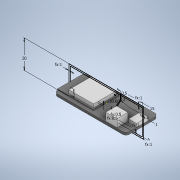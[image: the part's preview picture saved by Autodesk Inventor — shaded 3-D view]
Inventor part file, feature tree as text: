
AUTODESK INVENTOR PART (.ipt)
format: ipt  version: 2020 (Build 240168000, 168)  size: 187,904 bytes
history: native  units: in
note: dims shown in document units (in); Inventor stores cm internally (conversion verified against a paired STEP export)
features: extrude x6, sketch x2, fillet x1
ambient origin geometry x8: Origin, YZ Plane, XZ Plane, XY Plane, X Axis, Y Axis, Z Axis, Center Point
bodies: Solid1 (feature_tree)
feature tree (9):
  sketch  "Sketch1"  dims[d0=2.0079in d1=0.0689in d2=0.0315in]
  extrude  "PCB"  Depth=0.0689in
  fillet  "Fillet1"  Radius=0.0315in
  extrude  "ESP32PCB"  Depth=0.6949in
  extrude  "ESP32Shied"  Depth=0.0925in
  extrude  "Battery Connector"  Depth=0.9685in
  extrude  "Extrusion5"  Depth=0.315in
  extrude  "Extrusion6"  Depth=0.2165in
  sketch  "Sketch2"  dims[d3=1.0039in d4=0.6949in d5=0.0925in d6=0.9685in d7=0.315in d8=0.2165in d9=0.5807in d10=0.0984in d11=0.2224in d12=0.8996in d13=0.0in d14=0.7126in d15=0.0in d16=0.626in d17=0.0in d18=0.0984in d19=0.4331in d20=0.0in d21=0.1299in d22=0.0in d23=0.315in d24=0.0in d25=0.0039in d26=0.0394in d27=0.0394in d28=0.0394in d29=0.0394in d30=0.0394in d31=0.1969in d32=0.0394in d34=0.0394in d35=0.0394in d36=0.0197in d37=0.0197in d39=30.0deg d40=0.0197in d41=0.1575in d42=0.0787in d43=0.0787in d44=0.7874in d46=0.5906in d47=0.0197in d48=0.0344in d49=0.0197in d50=0.0344in]
